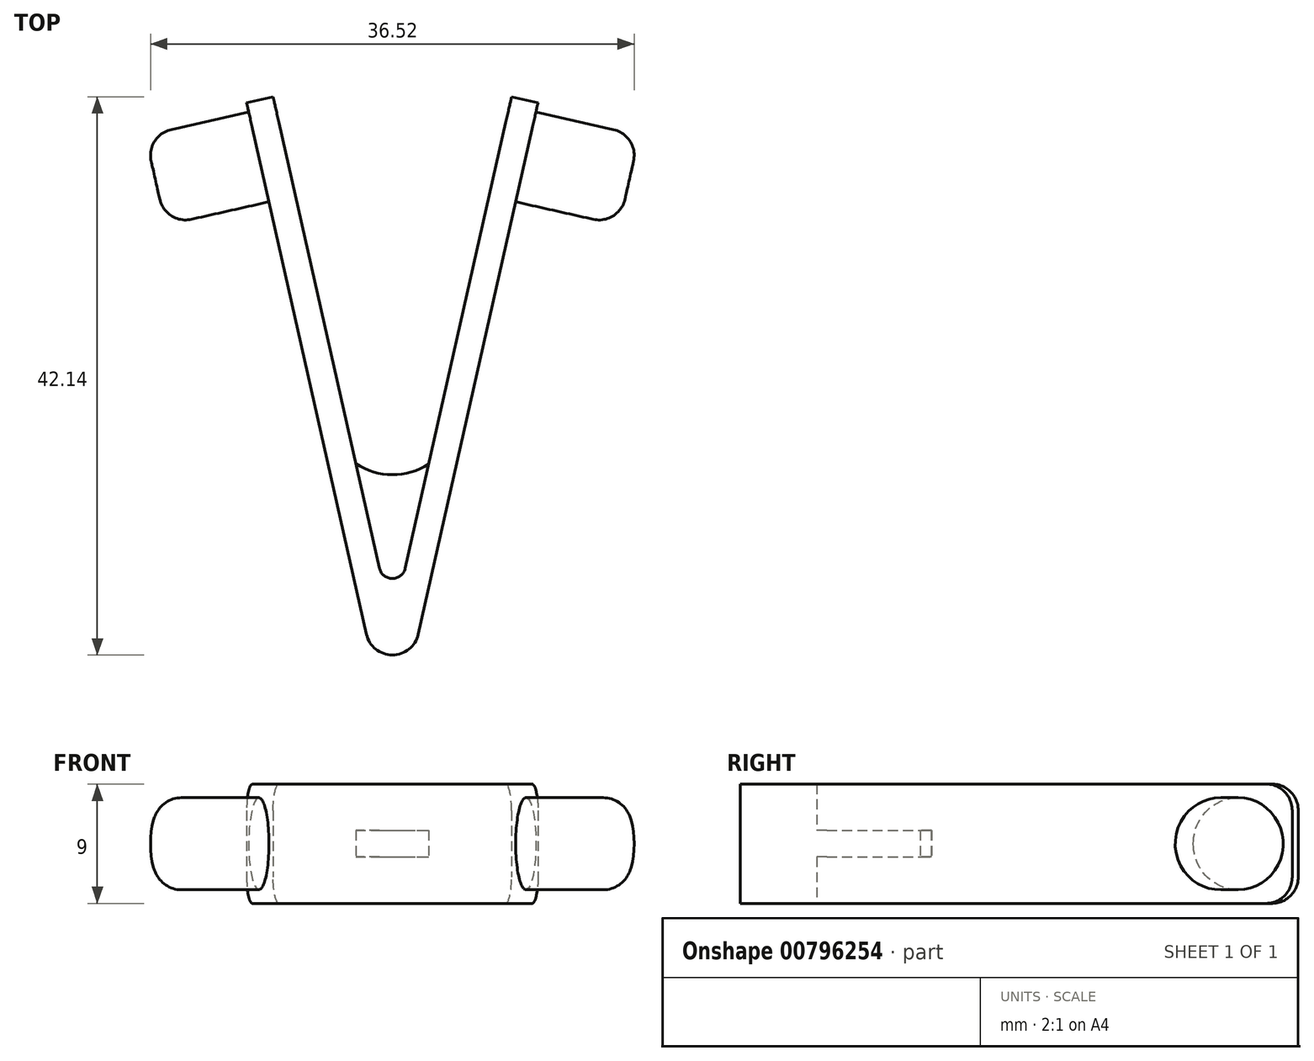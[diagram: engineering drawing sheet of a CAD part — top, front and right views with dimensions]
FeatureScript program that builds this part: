
annotation { "Feature Type Name" : "Feature", "Feature Type Description" : "" }
export const myFeature = defineFeature(function(context is Context, id is Id, definition is map)
    precondition{}
    {
        {
            var Q0;
            Q0=qCreatedBy(makeId("Top.planeOp"),FACE);
            var sketch = newSketch(context, id + "F0", { "sketchPlane" : qUnion([Q0])});
            skLineSegment(sketch, "E0", {"start": v(0, 0) * mm, "end": v(0, 32.5) * mm, "construction": true});
            skLineSegment(sketch, "E1", {"start": v(-1.95, -1.94) * mm, "end": v(-11, 38.18) * mm});
            skLineSegment(sketch, "E2", {"start": v(-11, 38.18) * mm, "end": v(-9, 38.64) * mm});
            skLineSegment(sketch, "E3", {"start": v(-9, 38.64) * mm, "end": v(-0.98, 3.05) * mm});
            skLineSegment(sketch, "E4.MirrorCS", {"start": v(9, 38.64) * mm, "end": v(0.98, 3.05) * mm});
            skLineSegment(sketch, "E5.MirrorCS", {"start": v(11, 38.18) * mm, "end": v(9, 38.64) * mm});
            skLineSegment(sketch, "E6.MirrorCS", {"start": v(1.95, -1.94) * mm, "end": v(11, 38.18) * mm});
            skPoint(sketch, "E7.trimOffspring.end.orphan", {"position": v(1.5, 0.74) * mm});
            skPoint(sketch, "E8.trimOffspring.end.orphan", {"position": v(-1.5, 0.74) * mm});
            skPoint(sketch, "E9.visualSharp", {"position": v(0, -1.27) * mm});
            skArc(sketch, "E9.filletArc", {"start": v(-0.98, 3.05) * mm, "mid": v(0, 2.27) * mm, "end": v(0.98, 3.05) * mm});
            skPoint(sketch, "E10.visualSharp", {"position": v(0, -10.6) * mm});
            skArc(sketch, "E10.filletArc", {"start": v(-1.95, -1.94) * mm, "mid": v(0, -3.5) * mm, "end": v(1.95, -1.94) * mm});
            skSolve(sketch);
        }
        {
            var Q0;
            Q0=makeQuery(id+"F0.imprint","IMPRINT",FACE,{"disambiguationData":[TD([[makeQuery(id+"F0.imprint","IMPRINT",EDGE,{"derivedFrom":sQuery(id+"F0.wireOp",EDGE,"E1")}),-1.0]])]});
            extrude(context, id + "F1", {"entities" : qUnion([Q0]), "depth" : 4.5 * mm, "offsetDistance" : 25 * mm, "hasSecondDirection" : true, "secondDirectionOppositeDirection" : true, "secondDirectionDepth" : 4.5 * mm});
        }
        {
            var Q0;
            Q0=qCreatedBy(makeId("Top.planeOp"),FACE);
            var sketch = newSketch(context, id + "F2", { "sketchPlane" : qUnion([Q0])});
            skLineSegment(sketch, "E11", {"start": v(-4.02, 12.17) * mm, "end": v(-1.8, -0.9) * mm});
            skLineSegment(sketch, "E12", {"start": v(-1.8, -0.9) * mm, "end": v(1.84, -0.9) * mm});
            skLineSegment(sketch, "E13", {"start": v(1.84, -0.9) * mm, "end": v(4.07, 12.17) * mm});
            skArc(sketch, "E14", {"start": v(-4.02, 12.17) * mm, "mid": v(0.02, 10.1) * mm, "end": v(4.07, 12.17) * mm});
            skSolve(sketch);
        }
        {
            var Q0;
            Q0=makeQuery(id+"F2.imprint","IMPRINT",FACE,{"disambiguationData":[TD([[makeQuery(id+"F2.imprint","IMPRINT",EDGE,{"derivedFrom":sQuery(id+"F2.wireOp",EDGE,"E11")}),1.0]])]});
            var Q1;
            Q1 = qConstructionFilter(qBodyType(qCreatedBy(id + "F2" ,EDGE), BodyType.WIRE), ConstructionObject.NO);
            extrude(context, id + "F3", {"entities" : qUnion([Q0]), "surfaceEntities" : qUnion([Q1]), "depth" : 1 * mm, "offsetDistance" : 25 * mm, "hasSecondDirection" : true, "secondDirectionOppositeDirection" : true, "secondDirectionDepth" : 1 * mm});
        }
        {
            var Q0;
            Q0=makeQuery(id+"F1.opExtrude","SWEPT_FACE",FACE,{"disambiguationData":[OSD([sQuery(id+"F0.wireOp",EDGE,"E6.MirrorCS")])]});
            var sketch = newSketch(context, id + "F4", { "sketchPlane" : qUnion([Q0])});
            skCircle(sketch, "E15", {"center": v(35.48, 0) * mm, "radius": 3.48 * mm});
            skPoint(sketch, "E15.centerSnap0", {"position": v(39.67, 0) * mm});
            skSolve(sketch);
        }
        {
            var Q0;
            Q0=makeQuery(id+"F4.imprint","IMPRINT",FACE,{"disambiguationData":[TD([[makeQuery(id+"F4.imprint","IMPRINT",EDGE,{"derivedFrom":sQuery(id+"F4.wireOp",EDGE,"E15")}),1.0]])]});
            extrude(context, id + "F5", {"entities" : qUnion([Q0]), "operationType" : NewBodyOperationType.ADD, "depth" : 8 * mm, "offsetDistance" : 25 * mm});
        }
        {
            var Q0;
            Q0=makeQuery(id+"F5.opExtrude","CAP_FACE",FACE,{"disambiguationData":[OSD([sQuery(id+"F4.wireOp",EDGE,"E15")])],"isStart":false});
            fillet(context, id + "F6", {"entities" : qUnion([Q0]), "radius" : 2 * mm, "tangentPropagation" : true, "allowEdgeOverflow" : false});
        }
        {
            var Q0;
            Q0=makeQuery(id+"F1.opExtrude","SWEPT_BODY",BODY,{"disambiguationData":[OSD([sQuery(id+"F0.wireOp",EDGE,"E1"),sQuery(id+"F0.wireOp",EDGE,"E2"),sQuery(id+"F0.wireOp",EDGE,"E3"),sQuery(id+"F0.wireOp",EDGE,"E4.MirrorCS"),sQuery(id+"F0.wireOp",EDGE,"E5.MirrorCS"),sQuery(id+"F0.wireOp",EDGE,"E6.MirrorCS"),sQuery(id+"F0.wireOp",EDGE,"E9.filletArc"),sQuery(id+"F0.wireOp",EDGE,"E10.filletArc")])]});
            var Q1;
            Q1=qCreatedBy(makeId("Right.planeOp"),FACE);
            mirror(context, id + "F7", {"operationType" : NewBodyOperationType.ADD, "entities" : qUnion([Q0]), "mirrorPlane" : qUnion([Q1])});
        }
        {
            var Q0;
            Q0=makeQuery(id+"F1.opExtrude","CAP_EDGE",EDGE,{"disambiguationData":[OSD([sQuery(id+"F0.wireOp",EDGE,"E5.MirrorCS")])],"isStart":false});
            var Q1;
            Q1=makeQuery(id+"F1.opExtrude","CAP_EDGE",EDGE,{"disambiguationData":[OSD([sQuery(id+"F0.wireOp",EDGE,"E5.MirrorCS")])],"isStart":true});
            var Q2;
            Q2=makeQuery(id+"F1.opExtrude","CAP_EDGE",EDGE,{"disambiguationData":[OSD([sQuery(id+"F0.wireOp",EDGE,"E2")])],"isStart":true});
            var Q3;
            Q3=makeQuery(id+"F1.opExtrude","CAP_EDGE",EDGE,{"disambiguationData":[OSD([sQuery(id+"F0.wireOp",EDGE,"E2")])],"isStart":false});
            fillet(context, id + "F8", {"entities" : qUnion([Q0, Q1, Q2, Q3]), "radius" : 2 * mm, "tangentPropagation" : true, "allowEdgeOverflow" : false});
        }
    });
